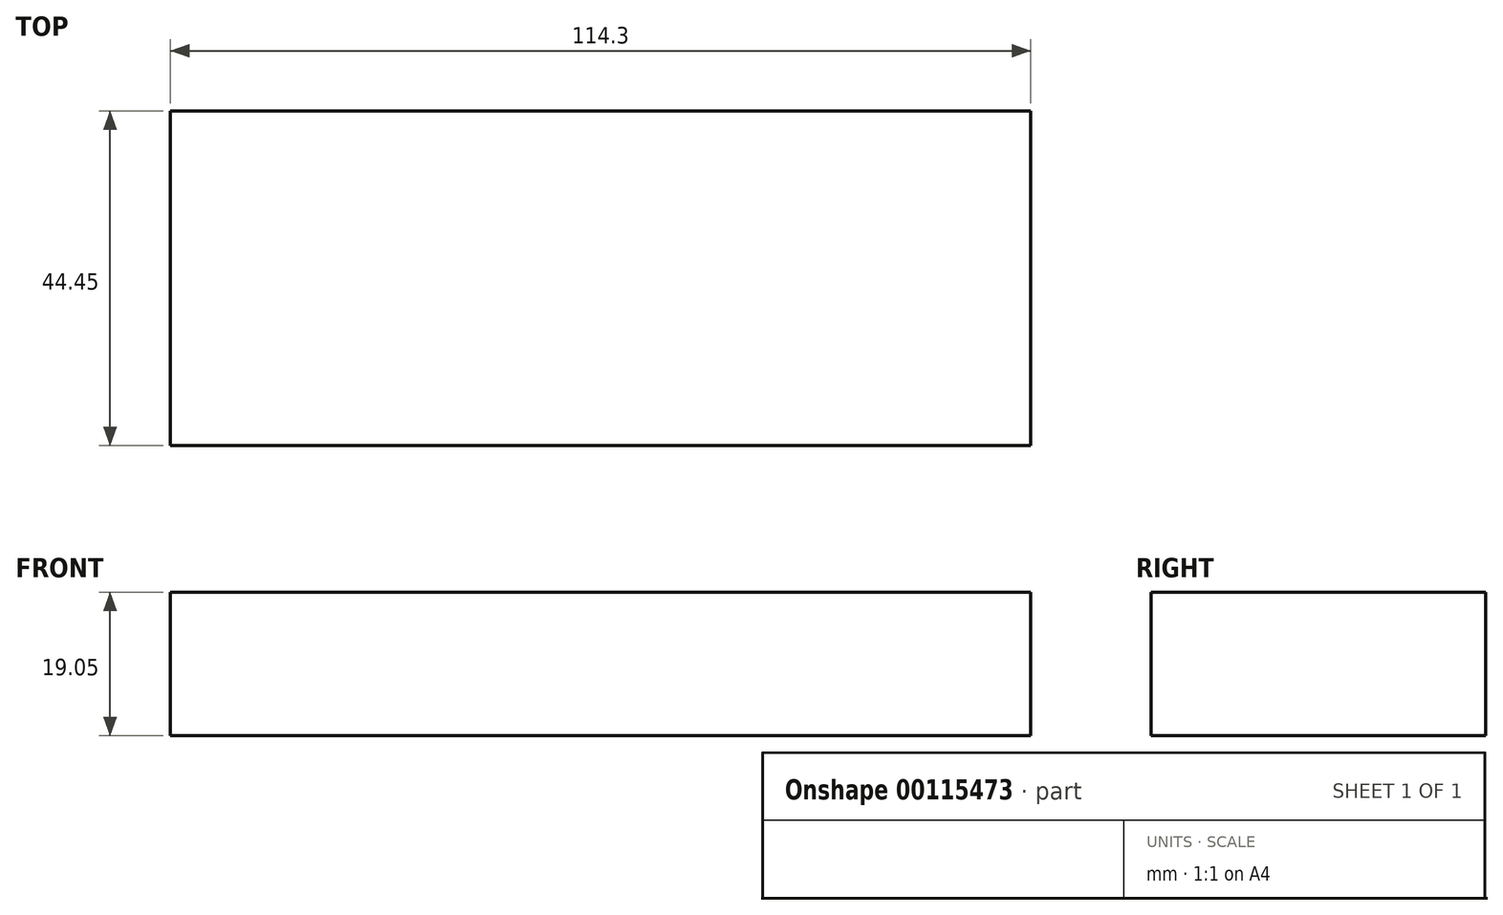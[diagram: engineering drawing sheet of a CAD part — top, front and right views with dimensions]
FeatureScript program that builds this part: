
annotation { "Feature Type Name" : "Feature", "Feature Type Description" : "" }
export const myFeature = defineFeature(function(context is Context, id is Id, definition is map)
    precondition{}
    {
        {
            var Q0;
            Q0=qCreatedBy(makeId("Top.planeOp"),FACE);
            var sketch = newSketch(context, id + "F0", { "sketchPlane" : qUnion([Q0])});
            skLineSegment(sketch, "E0.bottom", {"start": v(-31.97, 0) * mm, "end": v(82.33, 0) * mm});
            skLineSegment(sketch, "E0.top", {"start": v(-31.97, 44.45) * mm, "end": v(82.33, 44.45) * mm});
            skLineSegment(sketch, "E0.left", {"start": v(-31.97, 0) * mm, "end": v(-31.97, 44.45) * mm});
            skLineSegment(sketch, "E0.right", {"start": v(82.33, 0) * mm, "end": v(82.33, 44.45) * mm});
            skSolve(sketch);
        }
        {
            var Q0;
            Q0=makeQuery(id+"F0.imprint","IMPRINT",FACE,{"disambiguationData":[TD([[makeQuery(id+"F0.imprint","IMPRINT",EDGE,{"derivedFrom":sQuery(id+"F0.wireOp",EDGE,"E0.bottom")}),1.0]])]});
            extrude(context, id + "F1", {"entities" : qUnion([Q0]), "depth" : 19.05 * mm});
        }
    });
